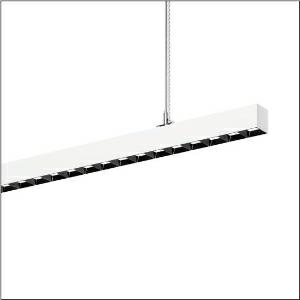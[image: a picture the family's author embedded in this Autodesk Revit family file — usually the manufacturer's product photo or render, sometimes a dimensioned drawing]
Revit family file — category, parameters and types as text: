
# Revit family: silica_r__21_51mx34dc3dwb_cbfc
name_source: partatom
category: Lighting Fixtures
units: mm (PartAtom-declared; Revit-internal decimal feet)

## family parameters
Cut with Voids When Loaded = No
Host = Face
Light Source = No
Part Type = Normal
Room Calculation Point = No
Round Connector Dimension = Use Diameter
Shared = No

## types (1)
- --- (1 x LED, 19200 lm, 129.1 W, 3000K)
    Apparent Load = 129 VA
    CIE Flux Codes = 74 94 99 56 100
    Color Rendering = 80
    Color Temperature = 3000K
    Default Elevation = 1800 mm
    Description = Silica® 21, office luminaire, primary light control with darklight reflector, of PMMA, black, light emission: direct/indirect distribution, primary light characteristic: asymmetric, installation type: suspended mounting, LED, rated luminous flux: 19.200lm, luminous efficacy: 149lm/W, light colour: 830, colour temperature: 3000K, with terminal, 3+2-pole, max. 2.5mm², mains connection: 220..240V, AC, 50/60Hz, rated input power: 129.1W, luminaire housing, of aluminium, traffic white (RAL 9016), length: 3.004mm, width: 53mm, height: 53mm, protection rating (complete): IP20, insulation class (complete): insulation class I (protective earthing), certification: CE, permissible operating ambient temperature: 0..+35°C, standard: EN 50419, packaging unit: 1 piece
    Height = 53 mm
    Lamp = 1 x LED
    Lamp Light Flux = 19200 lm
    Lamp Power = 129.1 W
    Lamp count = 1
    Length = 3004 mm
    Luminous efficacy = 149 lm/W
    Manufacturer = Siteco
    ModVariant = No
    Model = 51MX34DC3DWB
    Mounting Place = Ceiling
    Mounting Type = Pendant
    Number of Poles = 1
    OnlyDefault = Yes
    Power Factor = 1
    Product Name = Silica® 21
    Product group = office luminaire | ceiling pendant
    ProductGroupID = 905
    Protection Class = Protection class I
    Protection Degree = IP 20
    RLX_Detail_Level = 1
    RlxData = <blob elided: 66177 chars, md5=e8d00e2e>
    Socket = socket
    Standby Power = 0 W
    System Light Flux = 19200 lm
    System Power = 129 W
    Type Comments = factory setting: luminous flux: 100 % | dim-lin: 254 | 448 mA
    Type Image = l_1251637.jpg
    URL = http://relux.com
    VarID = @adj_029321
    Voltage = 0 V
    Weight = 0.00 kg
    Width = 53 mm

## geometry (parser evidence)
native form markers: Blend x4, Sweep x11
no freeform markers — native parametric forms only
